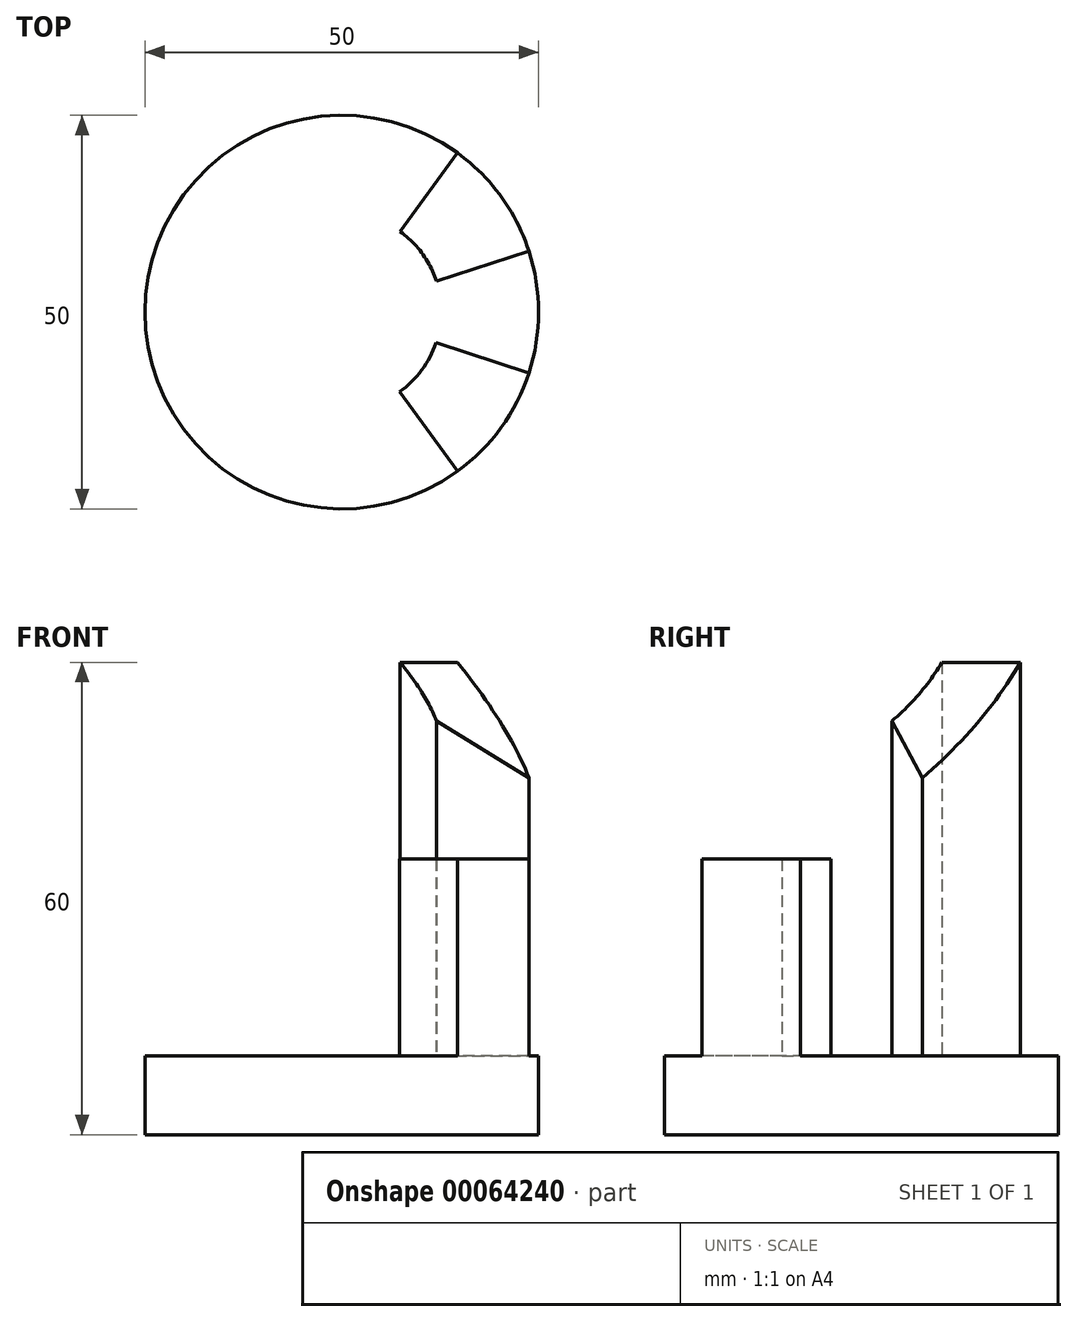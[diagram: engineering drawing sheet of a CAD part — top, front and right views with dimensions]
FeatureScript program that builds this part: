
annotation { "Feature Type Name" : "Feature", "Feature Type Description" : "" }
export const myFeature = defineFeature(function(context is Context, id is Id, definition is map)
    precondition{}
    {
        {
            var Q0;
            Q0=qCreatedBy(makeId("Top.planeOp"),FACE);
            var sketch = newSketch(context, id + "F0", { "sketchPlane" : qUnion([Q0])});
            skCircle(sketch, "E0", {"center": v(0, 0) * mm, "radius": 25 * mm, "construction": true});
            skCircle(sketch, "E1", {"center": v(0, 0) * mm, "radius": 25 * mm});
            skSolve(sketch);
        }
        {
            var Q0;
            Q0 = qSketchRegion(id + "F0", true);
            extrude(context, id + "F1", {"entities" : qUnion([Q0]), "depth" : 10 * mm});
        }
        {
            var Q0;
            Q0=makeQuery(id+"F1.opExtrude","CAP_FACE",FACE,{"disambiguationData":[OSD([sQuery(id+"F0.wireOp",EDGE,"E1")])],"isStart":false});
            var sketch = newSketch(context, id + "F2", { "sketchPlane" : qUnion([Q0])});
            skLineSegment(sketch, "E2", {"start": v(0, 37.84) * mm, "end": v(0, -25) * mm, "construction": true});
            skLineSegment(sketch, "E3", {"start": v(7.43, 10.22) * mm, "end": v(14.7, 20.23) * mm, "construction": true});
            skLineSegment(sketch, "E4", {"start": v(14.7, 20.23) * mm, "end": v(7.43, 10.22) * mm, "construction": true});
            skLineSegment(sketch, "E5", {"start": v(23.78, 7.73) * mm, "end": v(12.02, 3.9) * mm, "construction": true});
            skLineSegment(sketch, "E6", {"start": v(14.7, -20.23) * mm, "end": v(7.35, -10.11) * mm, "construction": true});
            skLineSegment(sketch, "E7", {"start": v(11.97, -3.89) * mm, "end": v(23.78, -7.73) * mm});
            skLineSegment(sketch, "E8", {"start": v(7.43, 10.22) * mm, "end": v(14.7, 20.23) * mm});
            skLineSegment(sketch, "E9", {"start": v(7.35, -10.11) * mm, "end": v(14.7, -20.23) * mm});
            skLineSegment(sketch, "E10", {"start": v(12.02, 3.9) * mm, "end": v(23.78, 7.73) * mm});
            skArc(sketch, "E11", {"start": v(23.78, 7.73) * mm, "mid": v(20.23, 14.7) * mm, "end": v(14.7, 20.23) * mm});
            skArc(sketch, "E12", {"start": v(14.7, -20.23) * mm, "mid": v(20.23, -14.7) * mm, "end": v(23.78, -7.73) * mm});
            skArc(sketch, "E13.trimOffspring", {"start": v(7.35, -10.11) * mm, "mid": v(10.15, -7.37) * mm, "end": v(11.97, -3.89) * mm});
            skArc(sketch, "E14.trimOffspring", {"start": v(12.02, 3.9) * mm, "mid": v(10.23, 7.43) * mm, "end": v(7.43, 10.22) * mm});
            skSolve(sketch);
        }
        {
            var Q0;
            Q0 = qSketchRegion(id + "F2", true);
            extrude(context, id + "F3", {"entities" : qUnion([Q0]), "operationType" : NewBodyOperationType.ADD, "depth" : 50 * mm});
        }
        {
            var Q0;
            Q0=makeQuery(id+"F3.opExtrude","CAP_EDGE",EDGE,{"disambiguationData":[OSD([sQuery(id+"F2.wireOp",EDGE,"E8")])],"isStart":false});
            cPlane(context, id + "F4", {"entities" : qUnion([Q0]), "cplaneType" : CPlaneType.LINE_ANGLE, "offset" : 150 * mm, "angle" : 45 * degree, "width" : 150 * mm, "height" : 150 * mm});
        }
        {
            var Q0;
            Q0=qCreatedBy(id+"F4.planeOp",FACE);
            var sketch = newSketch(context, id + "F5", { "sketchPlane" : qUnion([Q0])});
            skLineSegment(sketch, "E15.bottom", {"start": v(-24.24, 52.19) * mm, "end": v(3.66, 52.19) * mm});
            skLineSegment(sketch, "E15.top", {"start": v(-24.24, 28.24) * mm, "end": v(3.66, 28.24) * mm});
            skLineSegment(sketch, "E15.left", {"start": v(-24.24, 52.19) * mm, "end": v(-24.24, 28.24) * mm});
            skLineSegment(sketch, "E15.right", {"start": v(3.66, 52.19) * mm, "end": v(3.66, 28.24) * mm});
            skSolve(sketch);
        }
        {
            var Q0;
            Q0 = qSketchRegion(id + "F5", true);
            extrude(context, id + "F6", {"entities" : qUnion([Q0]), "operationType" : NewBodyOperationType.REMOVE, "depth" : 25 * mm});
        }
        {
            var Q0;
            Q0=makeQuery(id+"F3.opExtrude","CAP_FACE",FACE,{"disambiguationData":[OSD([sQuery(id+"F2.wireOp",EDGE,"E7"),sQuery(id+"F2.wireOp",EDGE,"E9"),sQuery(id+"F2.wireOp",EDGE,"E12"),sQuery(id+"F2.wireOp",EDGE,"E13.trimOffspring")])],"isStart":false});
            var sketch = newSketch(context, id + "F7", { "sketchPlane" : qUnion([Q0])});
            skLineSegment(sketch, "E16.bottom", {"start": v(0, 0) * mm, "end": v(26.92, 0) * mm});
            skLineSegment(sketch, "E16.top", {"start": v(0, -25.02) * mm, "end": v(26.92, -25.02) * mm});
            skLineSegment(sketch, "E16.left", {"start": v(0, 0) * mm, "end": v(0, -25.02) * mm});
            skLineSegment(sketch, "E16.right", {"start": v(26.92, 0) * mm, "end": v(26.92, -25.02) * mm});
            skSolve(sketch);
        }
        {
            var Q0;
            Q0 = qSketchRegion(id + "F7", true);
            extrude(context, id + "F8", {"entities" : qUnion([Q0]), "operationType" : NewBodyOperationType.REMOVE, "oppositeDirection" : true, "depth" : 25 * mm});
        }
    });
